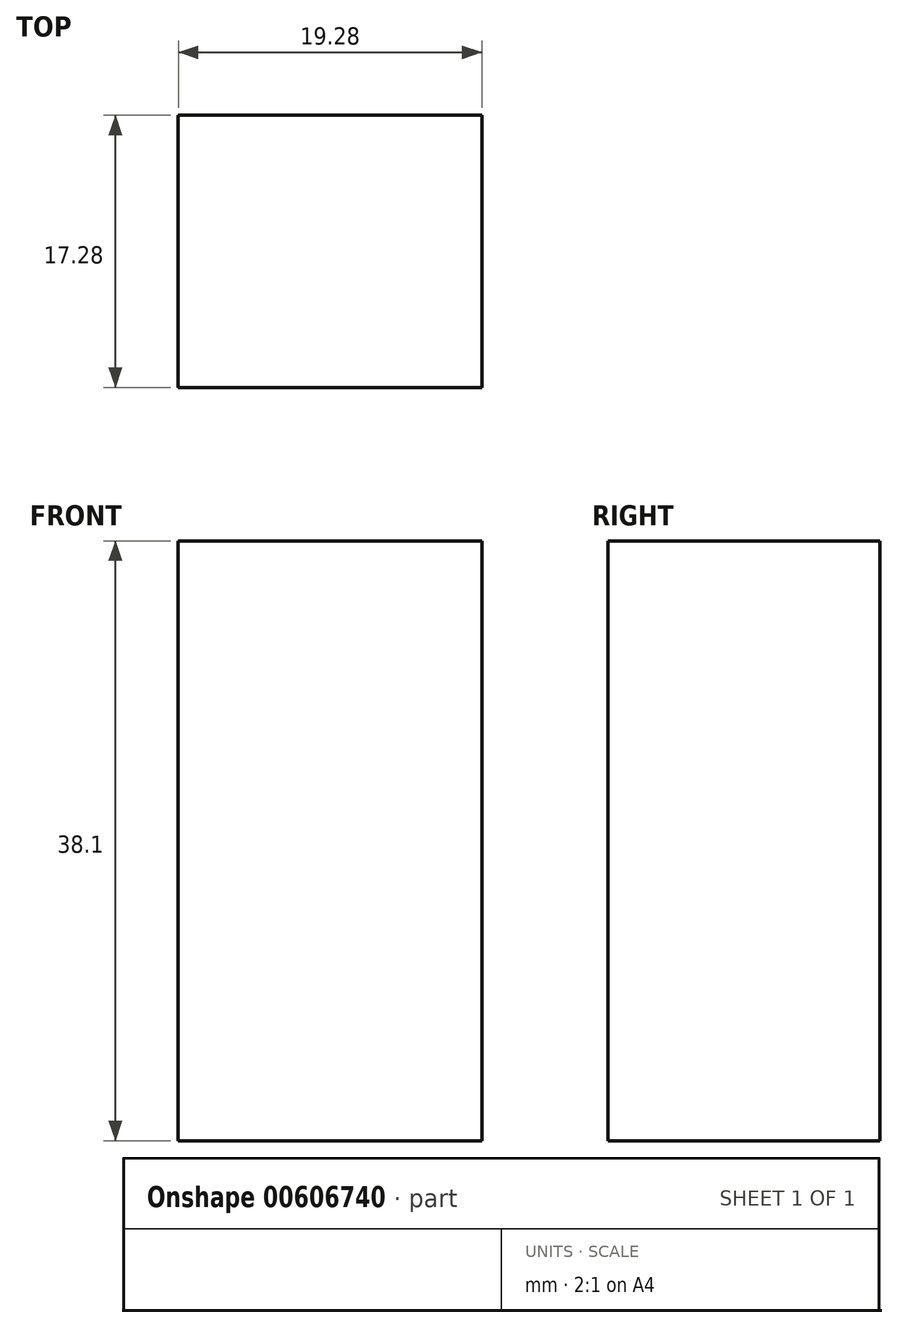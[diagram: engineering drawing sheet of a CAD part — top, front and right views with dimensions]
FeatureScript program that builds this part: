
annotation { "Feature Type Name" : "Feature", "Feature Type Description" : "" }
export const myFeature = defineFeature(function(context is Context, id is Id, definition is map)
    precondition{}
    {
        {
            var Q0;
            Q0=qCreatedBy(makeId("Top.planeOp"),FACE);
            var sketch = newSketch(context, id + "F0", { "sketchPlane" : qUnion([Q0])});
            skLineSegment(sketch, "E0.bottom", {"start": v(-37.81, -17.28) * mm, "end": v(-18.53, -17.28) * mm});
            skLineSegment(sketch, "E0.top", {"start": v(-37.81, 0) * mm, "end": v(-18.53, 0) * mm});
            skLineSegment(sketch, "E0.left", {"start": v(-37.81, -17.28) * mm, "end": v(-37.81, 0) * mm});
            skLineSegment(sketch, "E0.right", {"start": v(-18.53, -17.28) * mm, "end": v(-18.53, 0) * mm});
            skSolve(sketch);
        }
        {
            var Q0;
            Q0 = qSketchRegion(id + "F0", true);
            extrude(context, id + "F1", {"entities" : qUnion([Q0]), "depth" : 38.1 * mm, "offsetDistance" : 25.4 * mm});
        }
    });
